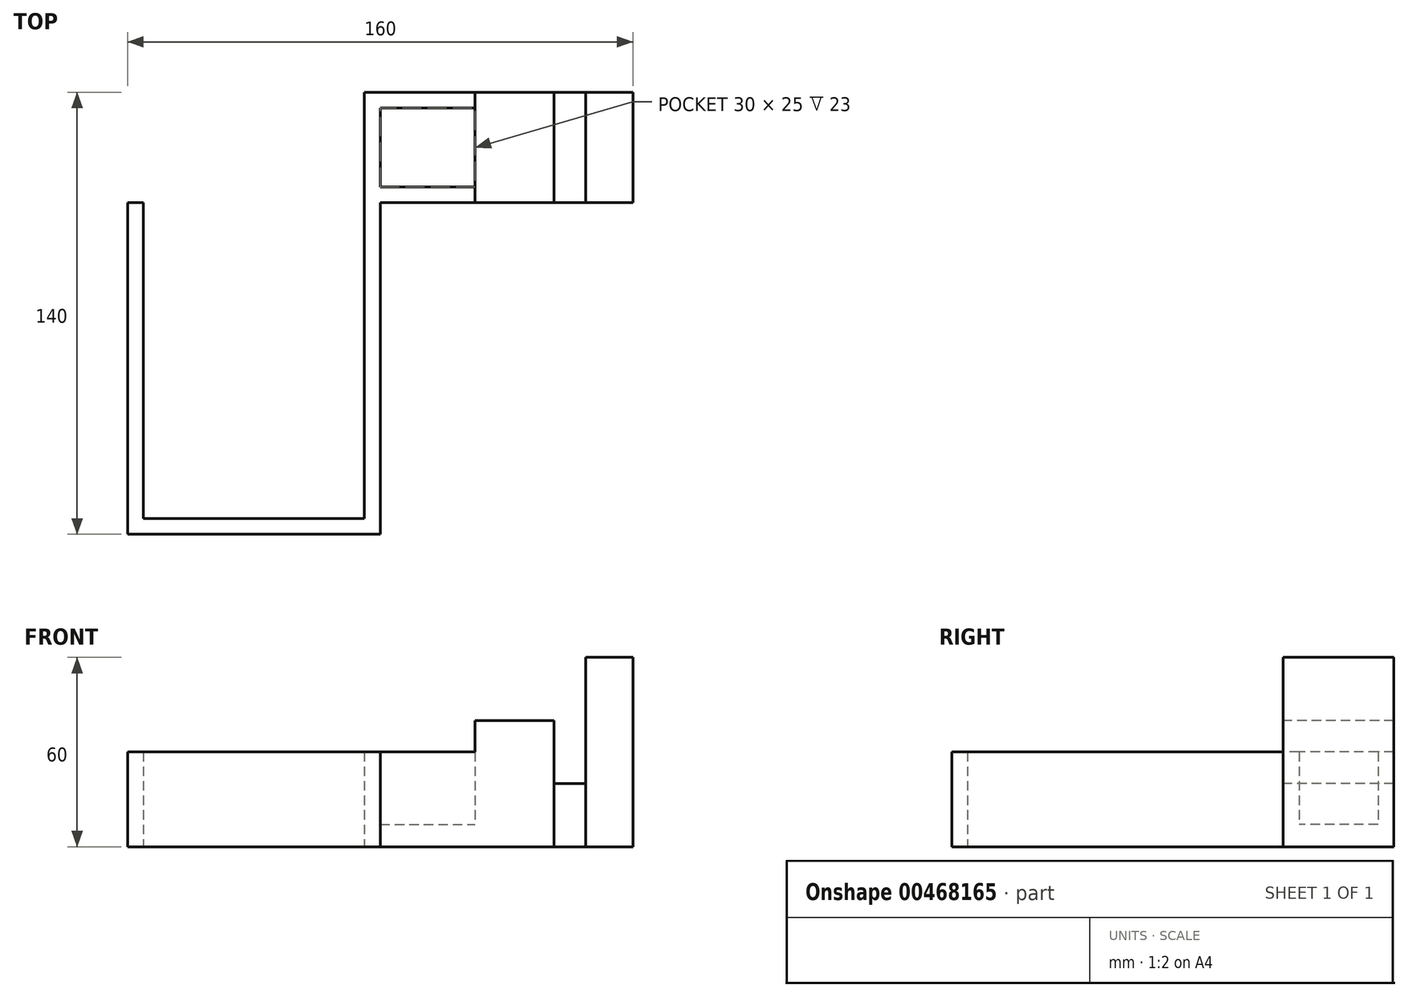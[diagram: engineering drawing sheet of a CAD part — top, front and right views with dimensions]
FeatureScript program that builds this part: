
annotation { "Feature Type Name" : "Feature", "Feature Type Description" : "" }
export const myFeature = defineFeature(function(context is Context, id is Id, definition is map)
    precondition{}
    {
        {
            var Q0;
            Q0=qCreatedBy(makeId("Top.planeOp"),FACE);
            var sketch = newSketch(context, id + "F0", { "sketchPlane" : qUnion([Q0])});
            skLineSegment(sketch, "E0.bottom", {"start": v(-75.09, 63.26) * mm, "end": v(84.91, 63.26) * mm});
            skLineSegment(sketch, "E0.top", {"start": v(-75.09, 28.26) * mm, "end": v(84.91, 28.26) * mm});
            skLineSegment(sketch, "E0.left", {"start": v(-75.09, 63.26) * mm, "end": v(-75.09, 28.26) * mm});
            skLineSegment(sketch, "E0.right", {"start": v(84.91, 63.26) * mm, "end": v(84.91, 28.26) * mm});
            skLineSegment(sketch, "E1.bottom", {"start": v(-75.09, 63.26) * mm, "end": v(4.91, 63.26) * mm});
            skLineSegment(sketch, "E1.top", {"start": v(-75.09, -76.74) * mm, "end": v(4.91, -76.74) * mm});
            skLineSegment(sketch, "E1.left", {"start": v(-75.09, 63.26) * mm, "end": v(-75.09, -76.74) * mm});
            skLineSegment(sketch, "E1.right", {"start": v(4.91, 63.26) * mm, "end": v(4.91, -76.74) * mm});
            skLineSegment(sketch, "E2", {"start": v(69.91, 63.26) * mm, "end": v(69.91, 28.26) * mm});
            skLineSegment(sketch, "E3", {"start": v(59.91, 63.26) * mm, "end": v(59.91, 28.26) * mm});
            skLineSegment(sketch, "E4", {"start": v(34.91, 63.26) * mm, "end": v(34.91, 28.26) * mm});
            skLineSegment(sketch, "E5.bottom", {"start": v(-70.09, 28.26) * mm, "end": v(-0.09, 28.26) * mm});
            skLineSegment(sketch, "E5.top", {"start": v(-70.09, -71.74) * mm, "end": v(-0.09, -71.74) * mm});
            skLineSegment(sketch, "E5.left", {"start": v(-70.09, 28.26) * mm, "end": v(-70.09, -71.74) * mm});
            skLineSegment(sketch, "E5.right", {"start": v(-0.09, 28.26) * mm, "end": v(-0.09, -71.74) * mm});
            skLineSegment(sketch, "E6", {"start": v(-70.09, 28.26) * mm, "end": v(-70.09, 63.26) * mm});
            skLineSegment(sketch, "E7", {"start": v(-0.09, 28.26) * mm, "end": v(-0.09, 63.26) * mm});
            skLineSegment(sketch, "E8", {"start": v(-75.09, 58.26) * mm, "end": v(84.91, 58.26) * mm});
            skLineSegment(sketch, "E9", {"start": v(-0.09, 33.26) * mm, "end": v(84.91, 33.26) * mm});
            skSolve(sketch);
        }
        {
            var Q0;
            {var subQ0=sQuery(id+"F0.wireOp",EDGE,"E1.left");var subQ1=sQuery(id+"F0.wireOp",EDGE,"E1.bottom");var subQ2=makeQuery(id+"F0.imprint","INTERSECT",VERTEX,{"derivedFrom":[subQ1,subQ0]});Q0=makeQuery(id+"F0.imprint","IMPRINT",FACE,{"disambiguationData":[TD([[makeQuery(id+"F0.imprint","IMPRINT",EDGE,{"disambiguationData":[TD([[subQ2,-1.0]])],"derivedFrom":subQ1}),-1.0]])]});}
            var Q1;
            {var subQ0=sQuery(id+"F0.wireOp",EDGE,"E1.left");var subQ1=sQuery(id+"F0.wireOp",EDGE,"E0.top");var subQ2=makeQuery(id+"F0.imprint","INTERSECT",VERTEX,{"derivedFrom":[subQ1,subQ0]});Q1=makeQuery(id+"F0.imprint","IMPRINT",FACE,{"disambiguationData":[TD([[makeQuery(id+"F0.imprint","IMPRINT",EDGE,{"disambiguationData":[TD([[subQ2,1.0]])],"derivedFrom":subQ0}),1.0]])]});}
            var Q2;
            {var subQ0=sQuery(id+"F0.wireOp",EDGE,"E1.top");Q2=makeQuery(id+"F0.imprint","IMPRINT",FACE,{"disambiguationData":[TD([[makeQuery(id+"F0.imprint","IMPRINT",EDGE,{"derivedFrom":subQ0}),1.0]])]});}
            var Q3;
            {var subQ0=sQuery(id+"F0.wireOp",EDGE,"E6");var subQ1=sQuery(id+"F0.wireOp",EDGE,"E1.bottom");var subQ2=makeQuery(id+"F0.imprint","INTERSECT",VERTEX,{"derivedFrom":[subQ1,subQ0]});Q3=makeQuery(id+"F0.imprint","IMPRINT",FACE,{"disambiguationData":[TD([[makeQuery(id+"F0.imprint","IMPRINT",EDGE,{"disambiguationData":[TD([[subQ2,-1.0]])],"derivedFrom":subQ1}),-1.0]])]});}
            var Q4;
            {var subQ1=sQuery(id+"F0.wireOp",EDGE,"E0.top");var subQ3=sQuery(id+"F0.wireOp",EDGE,"E1.right");var subQ4=makeQuery(id+"F0.imprint","INTERSECT",VERTEX,{"derivedFrom":[subQ1,subQ3]});Q4=makeQuery(id+"F0.imprint","IMPRINT",FACE,{"disambiguationData":[TD([[makeQuery(id+"F0.imprint","IMPRINT",EDGE,{"disambiguationData":[TD([[subQ4,1.0]])],"derivedFrom":subQ3}),-1.0]])]});}
            var Q5;
            {var subQ1=sQuery(id+"F0.wireOp",EDGE,"E1.bottom");var subQ3=sQuery(id+"F0.wireOp",EDGE,"E7");var subQ4=makeQuery(id+"F0.imprint","INTERSECT",VERTEX,{"derivedFrom":[subQ1,subQ3]});Q5=makeQuery(id+"F0.imprint","IMPRINT",FACE,{"disambiguationData":[TD([[makeQuery(id+"F0.imprint","IMPRINT",EDGE,{"disambiguationData":[TD([[subQ4,1.0]])],"derivedFrom":subQ3}),-1.0]])]});}
            extrude(context, id + "F1", {"entities" : qUnion([Q0, Q1, Q2, Q3, Q4, Q5]), "depth" : 30 * mm});
        }
        {
            var Q0;
            {var subQ4=sQuery(id+"F0.wireOp",EDGE,"E5.bottom");Q0=makeQuery(id+"F0.imprint","IMPRINT",FACE,{"disambiguationData":[TD([[makeQuery(id+"F0.imprint","IMPRINT",EDGE,{"derivedFrom":subQ4}),1.0]])]});}
            var Q1;
            Q1=makeQuery(id+"F0.imprint","IMPRINT",FACE,{"disambiguationData":[TD([[makeQuery(id+"F0.imprint","IMPRINT",EDGE,{"derivedFrom":sQuery(id+"F0.wireOp",EDGE,"E5.bottom")}),-1.0]])]});
            var Q2;
            {var subQ0=sQuery(id+"F0.wireOp",EDGE,"E8");var subQ1=sQuery(id+"F0.wireOp",EDGE,"E1.right");var subQ2=makeQuery(id+"F0.imprint","INTERSECT",VERTEX,{"derivedFrom":[subQ1,subQ0]});Q2=makeQuery(id+"F0.imprint","IMPRINT",FACE,{"disambiguationData":[TD([[makeQuery(id+"F0.imprint","IMPRINT",EDGE,{"disambiguationData":[TD([[subQ2,-1.0]])],"derivedFrom":subQ1}),-1.0]])]});}
            var Q3;
            {var subQ0=sQuery(id+"F0.wireOp",EDGE,"E8");var subQ1=sQuery(id+"F0.wireOp",EDGE,"E1.right");var subQ2=makeQuery(id+"F0.imprint","INTERSECT",VERTEX,{"derivedFrom":[subQ1,subQ0]});Q3=makeQuery(id+"F0.imprint","IMPRINT",FACE,{"disambiguationData":[TD([[makeQuery(id+"F0.imprint","IMPRINT",EDGE,{"disambiguationData":[TD([[subQ2,-1.0]])],"derivedFrom":subQ1}),1.0]])]});}
            extrude(context, id + "F2", {"entities" : qUnion([Q0, Q1, Q2, Q3]), "operationType" : NewBodyOperationType.ADD, "depth" : 7 * mm});
        }
        {
            var Q0;
            {var subQ1=sQuery(id+"F0.wireOp",EDGE,"E0.bottom");var subQ3=sQuery(id+"F0.wireOp",EDGE,"E4");var subQ4=makeQuery(id+"F0.imprint","INTERSECT",VERTEX,{"derivedFrom":[subQ1,subQ3]});Q0=makeQuery(id+"F0.imprint","IMPRINT",FACE,{"disambiguationData":[TD([[makeQuery(id+"F0.imprint","IMPRINT",EDGE,{"disambiguationData":[TD([[subQ4,-1.0]])],"derivedFrom":subQ3}),-1.0]])]});}
            var Q1;
            {var subQ0=sQuery(id+"F0.wireOp",EDGE,"E4");var subQ1=sQuery(id+"F0.wireOp",EDGE,"E0.top");var subQ2=makeQuery(id+"F0.imprint","INTERSECT",VERTEX,{"derivedFrom":[subQ1,subQ0]});Q1=makeQuery(id+"F0.imprint","IMPRINT",FACE,{"disambiguationData":[TD([[makeQuery(id+"F0.imprint","IMPRINT",EDGE,{"disambiguationData":[TD([[subQ2,1.0]])],"derivedFrom":subQ1}),1.0]])]});}
            extrude(context, id + "F3", {"entities" : qUnion([Q0, Q1]), "operationType" : NewBodyOperationType.ADD, "depth" : 30 * mm});
        }
        {
            var Q0;
            {var subQ0=sQuery(id+"F0.wireOp",EDGE,"E3");var subQ1=sQuery(id+"F0.wireOp",EDGE,"E0.bottom");var subQ2=makeQuery(id+"F0.imprint","INTERSECT",VERTEX,{"derivedFrom":[subQ1,subQ0]});Q0=makeQuery(id+"F0.imprint","IMPRINT",FACE,{"disambiguationData":[TD([[makeQuery(id+"F0.imprint","IMPRINT",EDGE,{"disambiguationData":[TD([[subQ2,1.0]])],"derivedFrom":subQ1}),-1.0]])]});}
            var Q1;
            {var subQ0=sQuery(id+"F0.wireOp",EDGE,"E8");var subQ1=sQuery(id+"F0.wireOp",EDGE,"E3");var subQ2=makeQuery(id+"F0.imprint","INTERSECT",VERTEX,{"derivedFrom":[subQ1,subQ0]});Q1=makeQuery(id+"F0.imprint","IMPRINT",FACE,{"disambiguationData":[TD([[makeQuery(id+"F0.imprint","IMPRINT",EDGE,{"disambiguationData":[TD([[subQ2,-1.0]])],"derivedFrom":subQ1}),-1.0]])]});}
            var Q2;
            {var subQ0=sQuery(id+"F0.wireOp",EDGE,"E3");var subQ1=sQuery(id+"F0.wireOp",EDGE,"E0.top");var subQ2=makeQuery(id+"F0.imprint","INTERSECT",VERTEX,{"derivedFrom":[subQ1,subQ0]});Q2=makeQuery(id+"F0.imprint","IMPRINT",FACE,{"disambiguationData":[TD([[makeQuery(id+"F0.imprint","IMPRINT",EDGE,{"disambiguationData":[TD([[subQ2,1.0]])],"derivedFrom":subQ1}),1.0]])]});}
            extrude(context, id + "F4", {"entities" : qUnion([Q0, Q1, Q2]), "operationType" : NewBodyOperationType.ADD, "depth" : 40 * mm});
        }
        {
            var Q0;
            {var subQ0=sQuery(id+"F0.wireOp",EDGE,"E0.right");var subQ1=sQuery(id+"F0.wireOp",EDGE,"E0.bottom");var subQ2=makeQuery(id+"F0.imprint","INTERSECT",VERTEX,{"derivedFrom":[subQ1,subQ0]});Q0=makeQuery(id+"F0.imprint","IMPRINT",FACE,{"disambiguationData":[TD([[makeQuery(id+"F0.imprint","IMPRINT",EDGE,{"disambiguationData":[TD([[subQ2,1.0]])],"derivedFrom":subQ1}),-1.0]])]});}
            var Q1;
            {var subQ0=sQuery(id+"F0.wireOp",EDGE,"E8");var subQ1=sQuery(id+"F0.wireOp",EDGE,"E0.right");var subQ2=makeQuery(id+"F0.imprint","INTERSECT",VERTEX,{"derivedFrom":[subQ1,subQ0]});Q1=makeQuery(id+"F0.imprint","IMPRINT",FACE,{"disambiguationData":[TD([[makeQuery(id+"F0.imprint","IMPRINT",EDGE,{"disambiguationData":[TD([[subQ2,-1.0]])],"derivedFrom":subQ1}),-1.0]])]});}
            var Q2;
            {var subQ0=sQuery(id+"F0.wireOp",EDGE,"E0.right");var subQ1=sQuery(id+"F0.wireOp",EDGE,"E0.top");var subQ2=makeQuery(id+"F0.imprint","INTERSECT",VERTEX,{"derivedFrom":[subQ1,subQ0]});Q2=makeQuery(id+"F0.imprint","IMPRINT",FACE,{"disambiguationData":[TD([[makeQuery(id+"F0.imprint","IMPRINT",EDGE,{"disambiguationData":[TD([[subQ2,1.0]])],"derivedFrom":subQ1}),1.0]])]});}
            extrude(context, id + "F5", {"entities" : qUnion([Q0, Q1, Q2]), "depth" : 60 * mm});
        }
        {
            var Q0;
            {var subQ0=sQuery(id+"F0.wireOp",EDGE,"E2");var subQ1=sQuery(id+"F0.wireOp",EDGE,"E0.bottom");var subQ2=makeQuery(id+"F0.imprint","INTERSECT",VERTEX,{"derivedFrom":[subQ1,subQ0]});Q0=makeQuery(id+"F0.imprint","IMPRINT",FACE,{"disambiguationData":[TD([[makeQuery(id+"F0.imprint","IMPRINT",EDGE,{"disambiguationData":[TD([[subQ2,1.0]])],"derivedFrom":subQ1}),-1.0]])]});}
            var Q1;
            {var subQ0=sQuery(id+"F0.wireOp",EDGE,"E8");var subQ1=sQuery(id+"F0.wireOp",EDGE,"E2");var subQ2=makeQuery(id+"F0.imprint","INTERSECT",VERTEX,{"derivedFrom":[subQ1,subQ0]});Q1=makeQuery(id+"F0.imprint","IMPRINT",FACE,{"disambiguationData":[TD([[makeQuery(id+"F0.imprint","IMPRINT",EDGE,{"disambiguationData":[TD([[subQ2,-1.0]])],"derivedFrom":subQ1}),-1.0]])]});}
            var Q2;
            {var subQ0=sQuery(id+"F0.wireOp",EDGE,"E2");var subQ1=sQuery(id+"F0.wireOp",EDGE,"E0.top");var subQ2=makeQuery(id+"F0.imprint","INTERSECT",VERTEX,{"derivedFrom":[subQ1,subQ0]});Q2=makeQuery(id+"F0.imprint","IMPRINT",FACE,{"disambiguationData":[TD([[makeQuery(id+"F0.imprint","IMPRINT",EDGE,{"disambiguationData":[TD([[subQ2,1.0]])],"derivedFrom":subQ1}),1.0]])]});}
            extrude(context, id + "F6", {"entities" : qUnion([Q0, Q1, Q2]), "depth" : 20 * mm});
        }
    });
